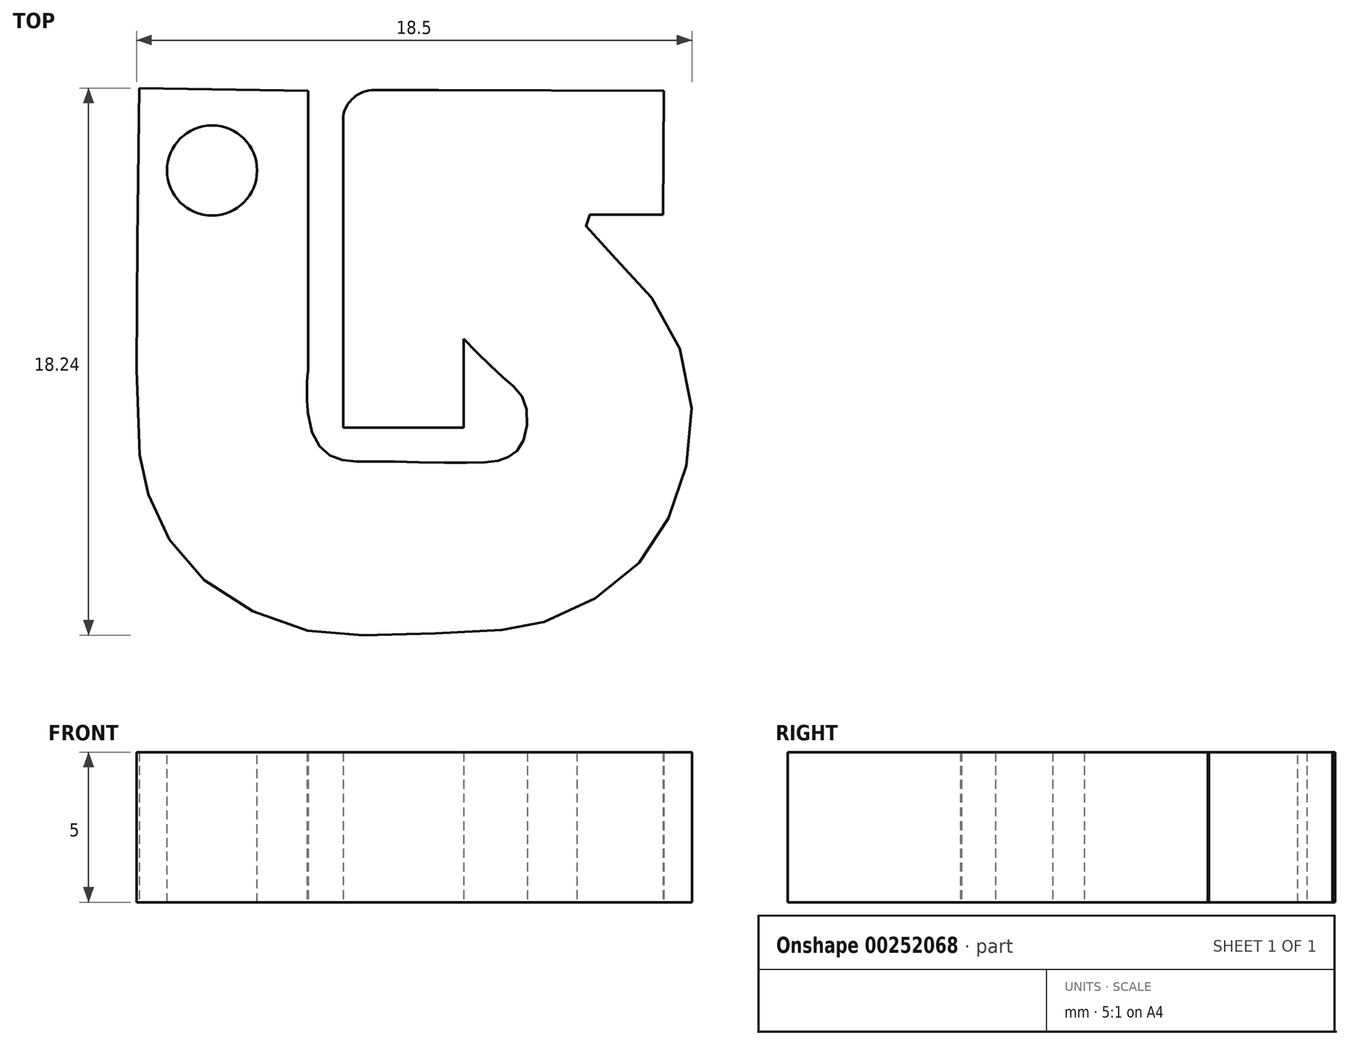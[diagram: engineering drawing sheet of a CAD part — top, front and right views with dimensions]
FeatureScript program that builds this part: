
annotation { "Feature Type Name" : "Feature", "Feature Type Description" : "" }
export const myFeature = defineFeature(function(context is Context, id is Id, definition is map)
    precondition{}
    {
        {
            var Q0;
            Q0=qCreatedBy(makeId("Top.planeOp"),FACE);
            var sketch = newSketch(context, id + "F0", { "sketchPlane" : qUnion([Q0])});
            skFitSpline(sketch, "E0", {"points": [v(10.9, 19.97) * mm, v(10.9, 7.83) * mm, v(11.18, 6.48) * mm, v(12.02, 4.72) * mm, v(13.7, 3.08) * mm, v(16.2, 1.95) * mm, v(18.75, 1.73) * mm, v(22.78, 1.89) * mm, v(24.28, 2.14) * mm, v(26.55, 3.27) * mm, v(28.15, 4.97) * mm, v(29.06, 7.17) * mm, v(29.25, 9.84) * mm, v(28.28, 12.55) * mm, v(26.77, 14.28) * mm, v(25.73, 15.4) * mm, v(25.48, 15.7) * mm, v(28.34, 15.75) * mm], "startDerivative": vector(-1.82, -119.3) * mm, "endDerivative": vector(61.66, 4.51) * mm});
            skLineSegment(sketch, "E1", {"start": v(28.37, 19.87) * mm, "end": v(28.34, 15.75) * mm});
            skLineSegment(sketch, "E2", {"start": v(20.86, 19.9) * mm, "end": v(28.37, 19.87) * mm});
            skLineSegment(sketch, "E3", {"start": v(20.86, 19.9) * mm, "end": v(18.72, 19.9) * mm});
            skArc(sketch, "E4", {"start": v(18.72, 19.9) * mm, "mid": v(18.04, 19.65) * mm, "end": v(17.68, 19.02) * mm});
            skLineSegment(sketch, "E5", {"start": v(17.68, 19.02) * mm, "end": v(17.68, 8.65) * mm});
            skLineSegment(sketch, "E6", {"start": v(17.68, 8.65) * mm, "end": v(21.7, 8.65) * mm});
            skLineSegment(sketch, "E7", {"start": v(21.7, 8.65) * mm, "end": v(21.7, 11.6) * mm});
            skFitSpline(sketch, "E8", {"points": [v(21.7, 11.6) * mm, v(23.06, 10.28) * mm, v(23.75, 9.46) * mm, v(23.66, 8.15) * mm, v(23.12, 7.64) * mm, v(22.18, 7.48) * mm, v(19, 7.52) * mm, v(17.5, 7.62) * mm, v(16.69, 8.4) * mm, v(16.56, 10.89) * mm], "startDerivative": vector(11.28, -11.59) * mm, "endDerivative": vector(2.65, 14.67) * mm});
            skLineSegment(sketch, "E9", {"start": v(16.52, 19.87) * mm, "end": v(16.51, 9.16) * mm});
            skLineSegment(sketch, "E10", {"start": v(10.9, 19.97) * mm, "end": v(16.52, 19.87) * mm});
            skSolve(sketch);
        }
        {
            var Q0;
            Q0=makeQuery(id+"F0.imprint","IMPRINT",FACE,{"disambiguationData":[TD([[makeQuery(id+"F0.imprint","IMPRINT",EDGE,{"derivedFrom":sQuery(id+"F0.wireOp",EDGE,"E0")}),1.0]])]});
            extrude(context, id + "F1", {"entities" : qUnion([Q0]), "endBound" : BoundingType.SYMMETRIC, "depth" : 5 * mm});
        }
        {
            var Q0;
            Q0=makeQuery(id+"F1.opExtrude","CAP_FACE",FACE,{"disambiguationData":[OSD([sQuery(id+"F0.wireOp",EDGE,"E0"),sQuery(id+"F0.wireOp",EDGE,"E1"),sQuery(id+"F0.wireOp",EDGE,"E2"),sQuery(id+"F0.wireOp",EDGE,"E3"),sQuery(id+"F0.wireOp",EDGE,"E4"),sQuery(id+"F0.wireOp",EDGE,"E5"),sQuery(id+"F0.wireOp",EDGE,"E6"),sQuery(id+"F0.wireOp",EDGE,"E7"),sQuery(id+"F0.wireOp",EDGE,"E8"),sQuery(id+"F0.wireOp",EDGE,"E9"),sQuery(id+"F0.wireOp",EDGE,"E10")])],"isStart":false});
            var sketch = newSketch(context, id + "F2", { "sketchPlane" : qUnion([Q0])});
            skCircle(sketch, "E11", {"center": v(13.32, 17.22) * mm, "radius": 1.9 * mm});
            skSolve(sketch);
        }
        {
            var Q0;
            Q0=sQuery(id+"F2.wireOp",VERTEX,"E11.center");
            var Q1;
            Q1=makeQuery(id+"F1.opExtrude","SWEPT_BODY",BODY,{"disambiguationData":[OSD([sQuery(id+"F0.wireOp",EDGE,"E0"),sQuery(id+"F0.wireOp",EDGE,"E1"),sQuery(id+"F0.wireOp",EDGE,"E2"),sQuery(id+"F0.wireOp",EDGE,"E3"),sQuery(id+"F0.wireOp",EDGE,"E4"),sQuery(id+"F0.wireOp",EDGE,"E5"),sQuery(id+"F0.wireOp",EDGE,"E6"),sQuery(id+"F0.wireOp",EDGE,"E7"),sQuery(id+"F0.wireOp",EDGE,"E8"),sQuery(id+"F0.wireOp",EDGE,"E9"),sQuery(id+"F0.wireOp",EDGE,"E10")])]});
            hole(context, id + "F3", {"style" : HoleStyle.SIMPLE, "endStyle" : HoleEndStyle.BLIND, "holeDiameter" : 3 * mm, "holeDepth" : 100 * mm, "tappedDepth" : 12 * mm, "tapClearance" : 3, "locations" : qUnion([Q0]), "scope" : qUnion([Q1])});
        }
    });
